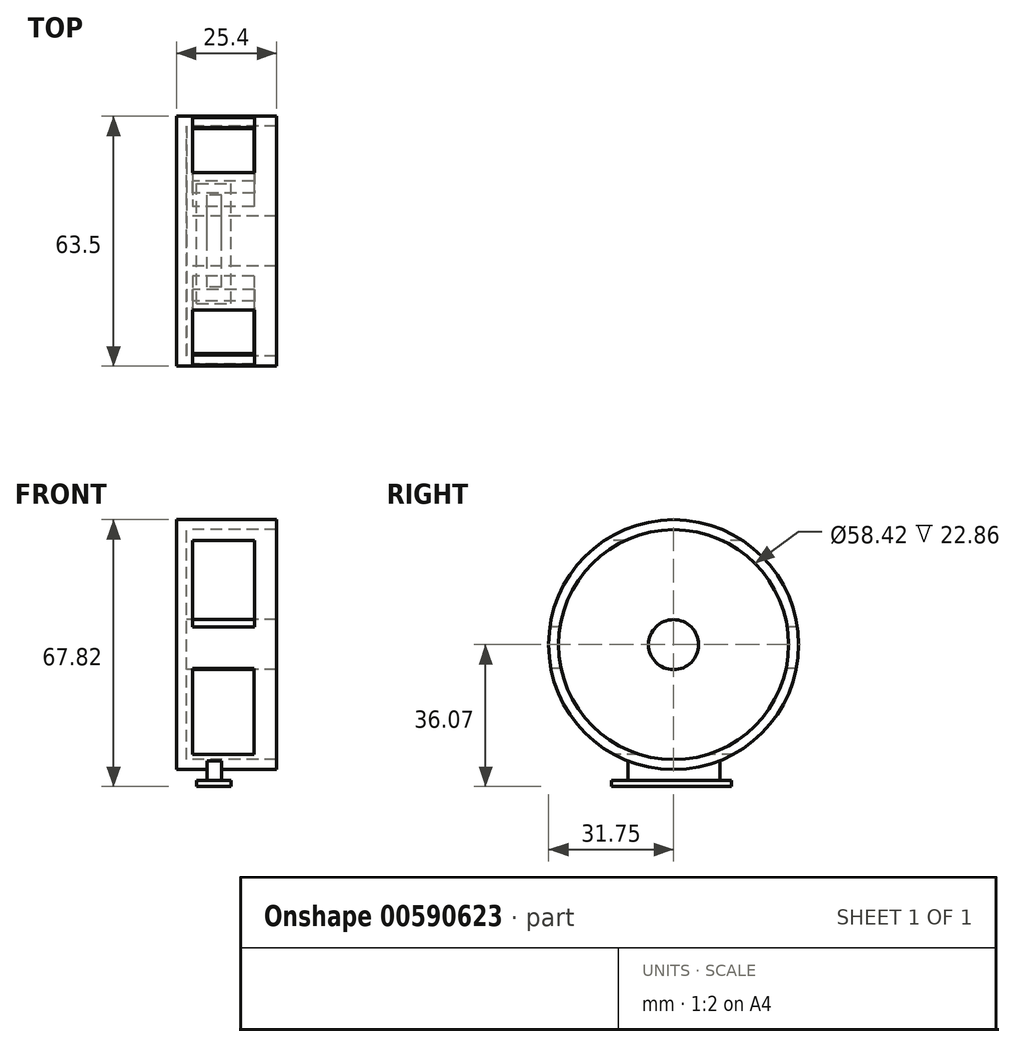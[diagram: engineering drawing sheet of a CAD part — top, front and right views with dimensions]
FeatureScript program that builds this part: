
annotation { "Feature Type Name" : "Feature", "Feature Type Description" : "" }
export const myFeature = defineFeature(function(context is Context, id is Id, definition is map)
    precondition{}
    {
        {
            var Q0;
            Q0=qCreatedBy(makeId("Right.planeOp"),FACE);
            var sketch = newSketch(context, id + "F0", { "sketchPlane" : qUnion([Q0])});
            skCircle(sketch, "E0", {"center": v(0, 0) * mm, "radius": 31.75 * mm});
            skSolve(sketch);
        }
        {
            var Q0;
            Q0=makeQuery(id+"F0.imprint","IMPRINT",FACE,{"disambiguationData":[TD([[makeQuery(id+"F0.imprint","IMPRINT",EDGE,{"derivedFrom":sQuery(id+"F0.wireOp",EDGE,"E0")}),1.0]])]});
            extrude(context, id + "F1", {"entities" : qUnion([Q0]), "depth" : 25.4 * mm, "offsetDistance" : 25.4 * mm});
        }
        {
            var Q0;
            Q0=makeQuery(id+"F1.opExtrude","CAP_FACE",FACE,{"disambiguationData":[OSD([sQuery(id+"F0.wireOp",EDGE,"E0")])],"isStart":false});
            shell(context, id + "F2", {"entities" : qUnion([Q0]), "thickness" : 2.54 * mm});
        }
        {
            var Q0;
            Q0=qCreatedBy(makeId("Front.planeOp"),FACE);
            var sketch = newSketch(context, id + "F3", { "sketchPlane" : qUnion([Q0])});
            skLineSegment(sketch, "E1.bottom", {"start": v(19.81, 26.51) * mm, "end": v(4.12, 26.51) * mm});
            skLineSegment(sketch, "E1.top", {"start": v(19.81, 4.5) * mm, "end": v(4.12, 4.5) * mm});
            skLineSegment(sketch, "E1.left", {"start": v(19.81, 26.51) * mm, "end": v(19.81, 4.5) * mm});
            skLineSegment(sketch, "E1.right", {"start": v(4.12, 26.51) * mm, "end": v(4.12, 4.5) * mm});
            skLineSegment(sketch, "E2.bottom", {"start": v(19.62, -6.03) * mm, "end": v(4.12, -6.03) * mm});
            skLineSegment(sketch, "E2.top", {"start": v(19.62, -27.85) * mm, "end": v(4.12, -27.85) * mm});
            skLineSegment(sketch, "E2.left", {"start": v(19.62, -6.03) * mm, "end": v(19.62, -27.85) * mm});
            skLineSegment(sketch, "E2.right", {"start": v(4.12, -6.03) * mm, "end": v(4.12, -27.85) * mm});
            skSolve(sketch);
        }
        {
            var Q0;
            Q0 = qSketchRegion(id + "F3", true);
            extrude(context, id + "F4", {"entities" : qUnion([Q0]), "operationType" : NewBodyOperationType.REMOVE, "endBound" : BoundingType.SYMMETRIC, "oppositeDirection" : true, "depth" : 116.33 * mm, "offsetDistance" : 25.4 * mm});
        }
        {
            var Q0;
            Q0=qCreatedBy(makeId("Top.planeOp"),FACE);
            cPlane(context, id + "F5", {"entities" : qUnion([Q0]), "cplaneType" : CPlaneType.OFFSET, "offset" : 29.2 * mm, "oppositeDirection" : true, "width" : 152.4 * mm, "height" : 152.4 * mm});
        }
        {
            var Q0;
            Q0=qCreatedBy(id+"F5.planeOp",FACE);
            var sketch = newSketch(context, id + "F6", { "sketchPlane" : qUnion([Q0])});
            skLineSegment(sketch, "E3.bottom", {"start": v(7.75, -11.58) * mm, "end": v(11.39, -11.58) * mm});
            skLineSegment(sketch, "E3.top", {"start": v(7.75, 11.77) * mm, "end": v(11.39, 11.77) * mm});
            skLineSegment(sketch, "E3.left", {"start": v(7.75, -11.58) * mm, "end": v(7.75, 11.77) * mm});
            skLineSegment(sketch, "E3.right", {"start": v(11.39, -11.58) * mm, "end": v(11.39, 11.77) * mm});
            skSolve(sketch);
        }
        {
            var Q0;
            Q0 = qSketchRegion(id + "F6", true);
            extrude(context, id + "F7", {"entities" : qUnion([Q0]), "operationType" : NewBodyOperationType.ADD, "oppositeDirection" : true, "depth" : 5.33 * mm, "offsetDistance" : 25.4 * mm});
        }
        {
            var Q0;
            Q0=makeQuery(id+"F7.opExtrude","CAP_FACE",FACE,{"disambiguationData":[OSD([sQuery(id+"F6.wireOp",EDGE,"E3.bottom"),sQuery(id+"F6.wireOp",EDGE,"E3.top"),sQuery(id+"F6.wireOp",EDGE,"E3.left"),sQuery(id+"F6.wireOp",EDGE,"E3.right")])],"isStart":false});
            var sketch = newSketch(context, id + "F8", { "sketchPlane" : qUnion([Q0])});
            skLineSegment(sketch, "E4.bottom", {"start": v(5.07, 15.8) * mm, "end": v(13.88, 15.8) * mm});
            skLineSegment(sketch, "E4.top", {"start": v(5.07, -14.64) * mm, "end": v(13.88, -14.64) * mm});
            skLineSegment(sketch, "E4.left", {"start": v(5.07, 15.8) * mm, "end": v(5.07, -14.64) * mm});
            skLineSegment(sketch, "E4.right", {"start": v(13.88, 15.8) * mm, "end": v(13.88, -14.64) * mm});
            skSolve(sketch);
        }
        {
            var Q0;
            Q0=makeQuery(id+"F8.imprint","IMPRINT",FACE,{"disambiguationData":[TD([[makeQuery(id+"F8.imprint","IMPRINT",EDGE,{"derivedFrom":sQuery(id+"F8.wireOp",EDGE,"E4.bottom")}),-1.0]])]});
            var Q1;
            Q1=makeQuery(id+"F8.imprint","IMPRINT",FACE,{"disambiguationData":[TD([[makeQuery(id+"F8.imprint","IMPRINT",EDGE,{"derivedFrom":makeQuery(id+"F7.opExtrude","CAP_EDGE",EDGE,{"disambiguationData":[OSD([sQuery(id+"F6.wireOp",EDGE,"E3.bottom")])],"isStart":false})}),-1.0]])]});
            extrude(context, id + "F9", {"entities" : qUnion([Q0, Q1]), "operationType" : NewBodyOperationType.ADD, "depth" : 1.52 * mm, "offsetDistance" : 25.4 * mm});
        }
        {
            var Q0;
            {var subQ0=sQuery(id+"F0.wireOp",EDGE,"E0");Q0=makeQuery(id+"F2.opShell","OFFSET_FACE",FACE,{"disambiguationData":[OSD([subQ0]),TDD([makeQuery(id+"F1.opExtrude","CAP_FACE",FACE,{"disambiguationData":[OSD([subQ0])],"isStart":true})])]});}
            var sketch = newSketch(context, id + "F10", { "sketchPlane" : qUnion([Q0])});
            skCircle(sketch, "E5", {"center": v(0, 0) * mm, "radius": 6.35 * mm});
            skSolve(sketch);
        }
        {
            var Q0;
            Q0=makeQuery(id+"F10.imprint","IMPRINT",FACE,{"disambiguationData":[TD([[makeQuery(id+"F10.imprint","IMPRINT",EDGE,{"derivedFrom":sQuery(id+"F10.wireOp",EDGE,"E5")}),1.0]])]});
            extrude(context, id + "F11", {"entities" : qUnion([Q0]), "operationType" : NewBodyOperationType.ADD, "depth" : 22.86 * mm, "offsetDistance" : 25.4 * mm});
        }
    });
